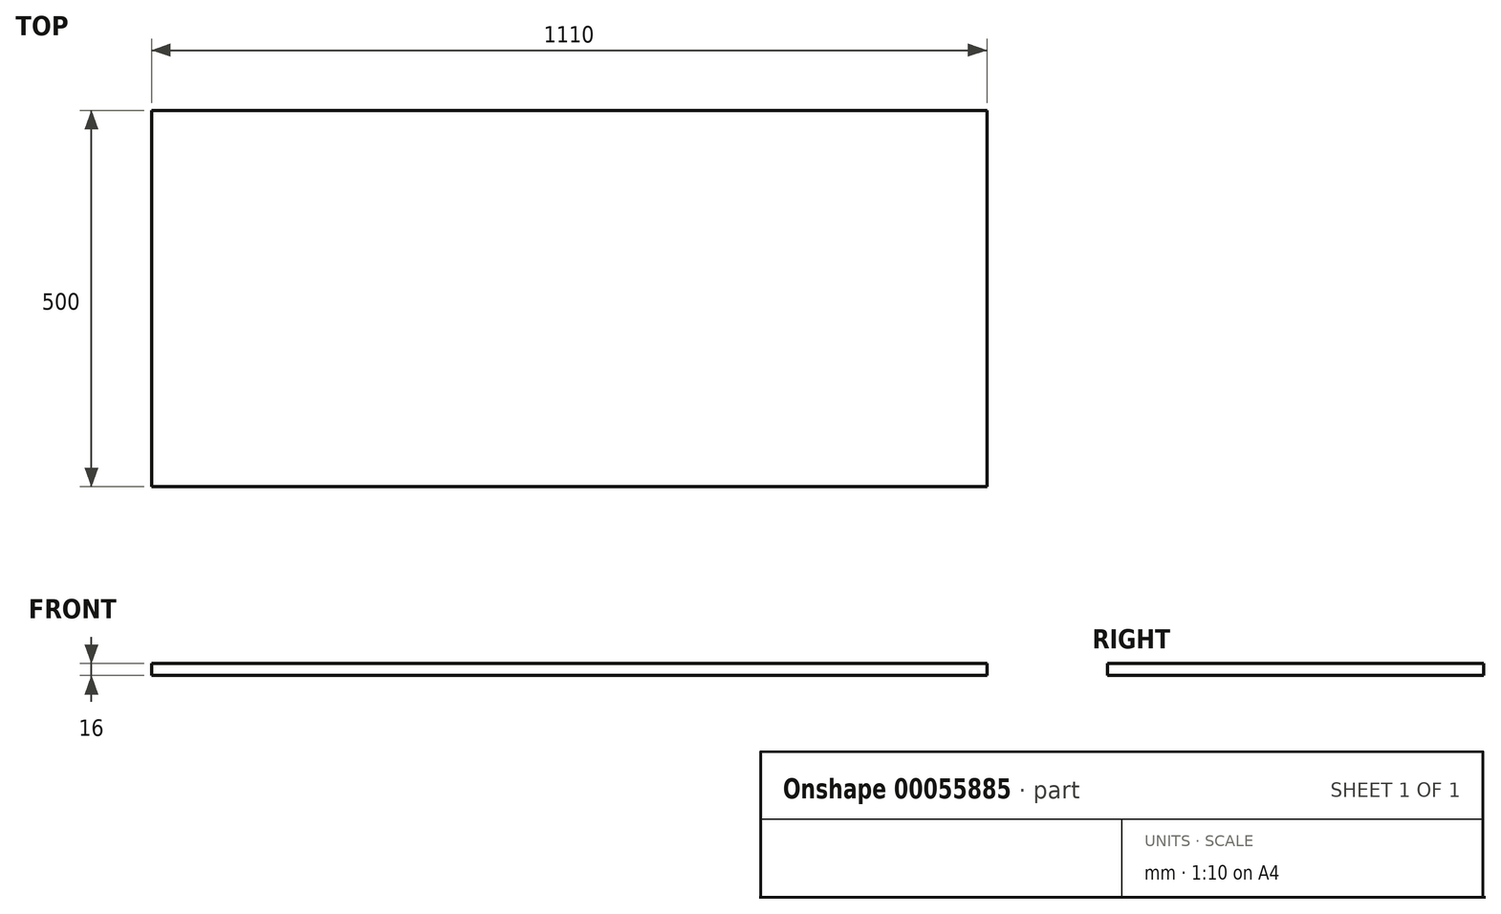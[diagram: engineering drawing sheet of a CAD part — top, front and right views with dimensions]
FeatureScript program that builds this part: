
annotation { "Feature Type Name" : "Feature", "Feature Type Description" : "" }
export const myFeature = defineFeature(function(context is Context, id is Id, definition is map)
    precondition{}
    {
        {
            var Q0;
            Q0=qCreatedBy(makeId("Top.planeOp"),FACE);
            var sketch = newSketch(context, id + "F0", { "sketchPlane" : qUnion([Q0])});
            skLineSegment(sketch, "E0.rect.bottom", {"start": v(-555, 250) * mm, "end": v(555, 250) * mm});
            skLineSegment(sketch, "E0.rect.top", {"start": v(-555, -250) * mm, "end": v(555, -250) * mm});
            skLineSegment(sketch, "E0.rect.left", {"start": v(-555, 250) * mm, "end": v(-555, -250) * mm});
            skLineSegment(sketch, "E0.rect.right", {"start": v(555, 250) * mm, "end": v(555, -250) * mm});
            skPoint(sketch, "E0.rect.middle", {"position": v(0, 0) * mm});
            skSolve(sketch);
        }
        {
            var Q0;
            Q0=makeQuery(id+"F0.imprint","IMPRINT",FACE,{"disambiguationData":[TD([[makeQuery(id+"F0.imprint","IMPRINT",EDGE,{"derivedFrom":sQuery(id+"F0.wireOp",EDGE,"E0.rect.bottom")}),-1.0]])]});
            extrude(context, id + "F1", {"entities" : qUnion([Q0]), "oppositeDirection" : true, "depth" : 16 * mm});
        }
    });
